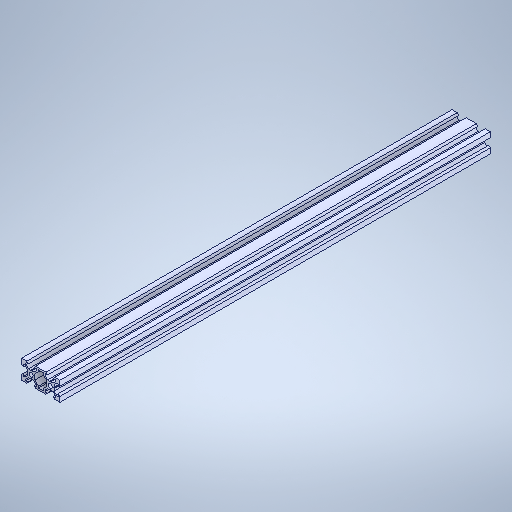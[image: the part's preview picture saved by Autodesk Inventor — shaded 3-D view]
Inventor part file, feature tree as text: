
AUTODESK INVENTOR PART (.ipt)
format: ipt  version: 2025.2 (Build 292293000, 293)  size: 360,960 bytes
history: native  units: in
note: dims shown in document units (in); Inventor stores cm internally (conversion verified against a paired STEP export)
features: extrude x1, sketch x1, other x1
ambient origin geometry x8: Origin, YZ Plane, XZ Plane, XY Plane, X Axis, Y Axis, Z Axis, Center Point
bodies: Solid1 (feature_tree)
feature tree (3):
  extrude  "Extrusion1"  [1 undecoded]
  sketch  "Sketch1"  dims[d0=1.9685in d1=0.0in]
  other  "Boss-Extrude1"
note: 1 required parameter value undecoded (feature->parameter linkage not recoverable at this tier; creation-order binding heuristic only, values carry confidence <= 0.55)
